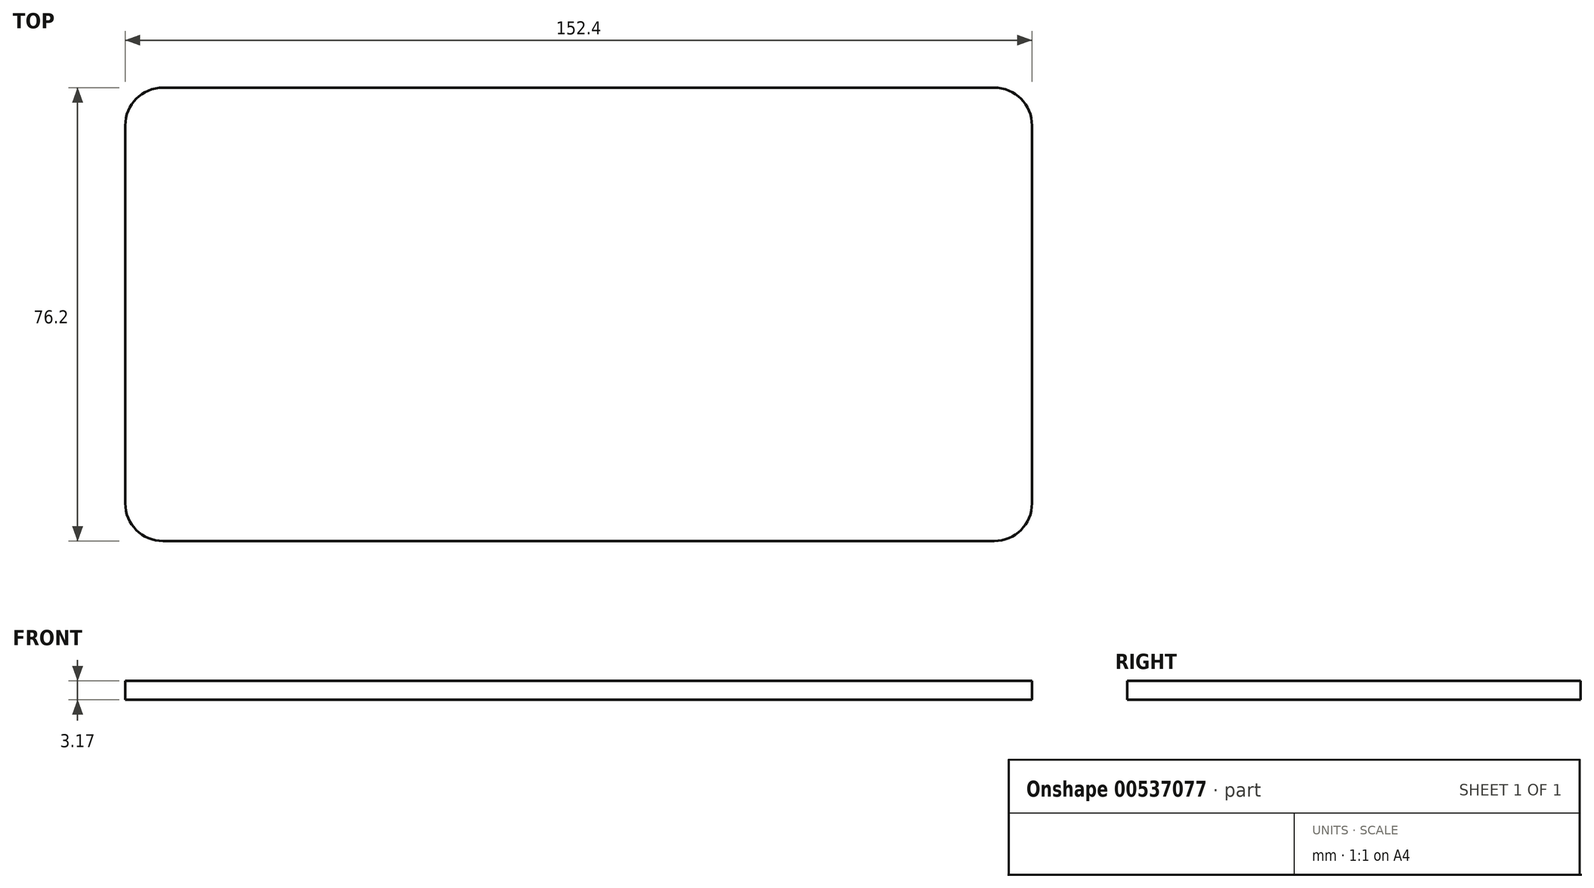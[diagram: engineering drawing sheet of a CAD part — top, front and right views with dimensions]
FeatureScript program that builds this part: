
annotation { "Feature Type Name" : "Feature", "Feature Type Description" : "" }
export const myFeature = defineFeature(function(context is Context, id is Id, definition is map)
    precondition{}
    {
        {
            var Q0;
            Q0=qCreatedBy(makeId("Top.planeOp"),FACE);
            var sketch = newSketch(context, id + "F0", { "sketchPlane" : qUnion([Q0])});
            skLineSegment(sketch, "E0.bottom", {"start": v(76.2, -38.1) * mm, "end": v(-76.2, -38.1) * mm});
            skLineSegment(sketch, "E0.top", {"start": v(76.2, 38.1) * mm, "end": v(-76.2, 38.1) * mm});
            skLineSegment(sketch, "E0.left", {"start": v(76.2, -38.1) * mm, "end": v(76.2, 38.1) * mm});
            skLineSegment(sketch, "E0.right", {"start": v(-76.2, -38.1) * mm, "end": v(-76.2, 38.1) * mm});
            skPoint(sketch, "E0.middle", {"position": v(0, 0) * mm});
            skSolve(sketch);
        }
        {
            var Q0;
            Q0=makeQuery(id+"F0.imprint","IMPRINT",FACE,{"disambiguationData":[TD([[makeQuery(id+"F0.imprint","IMPRINT",EDGE,{"derivedFrom":sQuery(id+"F0.wireOp",EDGE,"E0.bottom")}),-1.0]])]});
            extrude(context, id + "F1", {"entities" : qUnion([Q0]), "oppositeDirection" : true, "depth" : 3.17 * mm, "offsetDistance" : 25.4 * mm});
        }
        {
            var Q0;
            Q0=makeQuery(id+"F1.opExtrude","SWEPT_EDGE",EDGE,{"disambiguationData":[OSD([sQuery(id+"F0.wireOp",EDGE,"E0.bottom"),sQuery(id+"F0.wireOp",EDGE,"E0.right")])]});
            var Q1;
            Q1=makeQuery(id+"F1.opExtrude","SWEPT_EDGE",EDGE,{"disambiguationData":[OSD([sQuery(id+"F0.wireOp",EDGE,"E0.bottom"),sQuery(id+"F0.wireOp",EDGE,"E0.left")])]});
            var Q2;
            Q2=makeQuery(id+"F1.opExtrude","SWEPT_EDGE",EDGE,{"disambiguationData":[OSD([sQuery(id+"F0.wireOp",EDGE,"E0.top"),sQuery(id+"F0.wireOp",EDGE,"E0.left")])]});
            var Q3;
            Q3=makeQuery(id+"F1.opExtrude","SWEPT_EDGE",EDGE,{"disambiguationData":[OSD([sQuery(id+"F0.wireOp",EDGE,"E0.top"),sQuery(id+"F0.wireOp",EDGE,"E0.right")])]});
            fillet(context, id + "F2", {"entities" : qUnion([Q0, Q1, Q2, Q3]), "radius" : 6.35 * mm, "tangentPropagation" : true, "allowEdgeOverflow" : false});
        }
    });
